# Revit family: Speaker-Indoor_OutDoor_WaterProof-Panasonic-LB301X
name_source: partatom
category: Communication Devices
units: mm (PartAtom-declared; Revit-internal decimal feet)

## family parameters
Cut with Voids When Loaded = No
Host = Face
Maintain Annotation Orientation = Yes
OmniClass Number = 23.85.10.11.14.14.14
OmniClass Title = Loudspeakers
Part Type = Normal
Room Calculation Point = No
Round Connector Dimension = Use Diameter
Shared = No

## types (1)
- WS-LB301
    Body Depth = 160 mm  [stored 0.524934 ft]
    Bracket Depth = 31 mm  [stored 0.101706 ft]
    Bracket Edge Radius = 15.5 mm  [stored 0.050853 ft]
    Bracket Height = 61.8 mm
    Bracket Inner Depth = 122 mm  [stored 0.400262 ft]
    Bracket Width = 128 mm  [stored 0.419948 ft]
    Coverage = 105° x 100°
    Date Last Modified = 2023/03/01
    Default Elevation = 2700 mm  [stored 8.85827 ft]
    Depth = 200 mm  [stored 0.656168 ft]
    Description = 全天候型スピーカーシステム＜７．５Ｗ／１５Ｗ／３０Ｗ＞WS-LB301
    Equipment Abbreviation = SP
    Family Version = 1.0.0
    Finish = エンクロージャー（前面パネル、キャビネット） ：PP樹脂、白色半艶塗装 （マンセルN9近似色）/ スピーカー取付金具、固定金具、外郭ねじ類 ：ステンレス
    Frequency characteristic = 70 Hz ～ 18 kHz（-20 dB）
    Front Body Height = 158 mm
    Front Body Width = 158 mm
    Grill Material = Plastic - Panasonic - SP White
    Height = 293 mm
    Input Impedance = ハイインピーダンス（Hi） ：330 Ω（30 W）、670 Ω（15 W）、1.3 KΩ（7.5 W） / ローインピーダンス（Lo） ：8 Ω （切替スイッチおよび接続スピーカーケーブルにより切り替え）
    Input connector = スピーカーケーブル
    Manufacturer = Panasonic Connect Co., Ltd.
    Model = 全天候型スピーカーシステム＜７．５Ｗ／１５Ｗ／３０Ｗ＞WS-LB301
    Model Disclaimer = Contact Panasonic for more information
    Offset for Pan Axis and Tilt Axis = 134 mm
    Operational Temperature = -20 ℃～ +60 ℃
    Pan Axis Offset = 100 mm  [stored 0.328084 ft]
    Part Description = 全天候型スピーカーシステム＜７．５Ｗ／１５Ｗ／３０Ｗ＞WS-LB301
    Part Number = WS-LB301
    Power Handling = －
    Product Documentation Link = https://solpartner.jpn.panasonic.com
    Product Material = Plastic - Panasonic - SP White
    Product Page URL = https://connect.panasonic.com
    Rated Input = 30 W、15 W、7.5 W
    Rear Body Height = 122 mm  [stored 0.400262 ft]
    Rear Body Width = 122 mm  [stored 0.400262 ft]
    SPL = 90 dB （1 m／1 W）
    SV Visible = No
    Sound Power Level = 90
    Speaker Front Offset = 80.2 mm  [stored 0.263123 ft]
    Speaker Type = 301
    Speaker unit = 12cmダイナミックウーハー、2cmツィーター
    Tilt  Handle Length = 1000 mm  [stored 3.28084 ft]
    Type = 2ウェイ密閉型
    URL = https://biz.panasonic.com
    View Volume Material = Panasonic - ViewVolume
    Weight = 4.80 kgf
    Width = 155 mm  [stored 0.50853 ft]

note: [stored X ft] marks values corroborated as IEEE doubles in the binary element streams (Revit-internal decimal feet)

## geometry (parser evidence)
native form markers: Blend x2, Sweep x11
no freeform markers — native parametric forms only
